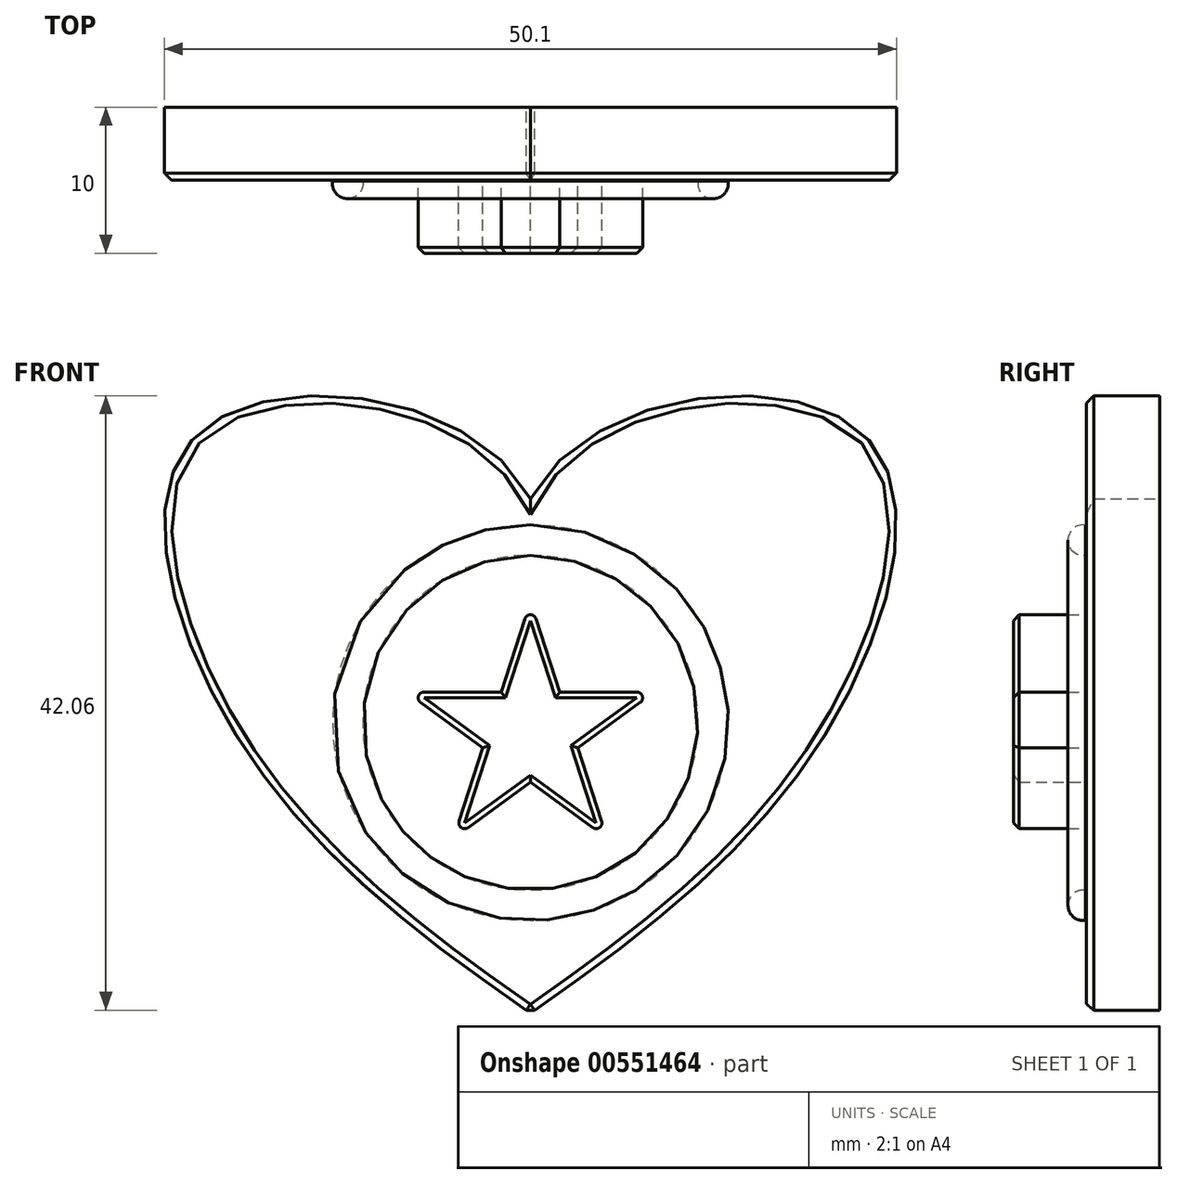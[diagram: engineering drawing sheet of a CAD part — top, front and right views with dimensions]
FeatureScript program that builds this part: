
annotation { "Feature Type Name" : "Feature", "Feature Type Description" : "" }
export const myFeature = defineFeature(function(context is Context, id is Id, definition is map)
    precondition{}
    {
        {
            var Q0;
            Q0=qCreatedBy(makeId("Front.planeOp"),FACE);
            var sketch = newSketch(context, id + "F0", { "sketchPlane" : qUnion([Q0])});
            skFitSpline(sketch, "E0", {"points": [v(0, 4.74) * mm, v(-22.34, 9.53) * mm, v(-20.92, -10.1) * mm, v(0, -30.47) * mm], "startDerivative": vector(-35.89, 67.68) * mm, "endDerivative": vector(70.46, -48.53) * mm});
            skFitSpline(sketch, "E1.MirrorCS", {"points": [v(0, 4.74) * mm, v(22.34, 9.53) * mm, v(20.92, -10.1) * mm, v(0, -30.47) * mm], "startDerivative": vector(35.89, 67.68) * mm, "endDerivative": vector(-70.46, -48.53) * mm});
            skPoint(sketch, "E2", {"position": v(-25, 1.75) * mm});
            skPoint(sketch, "E3", {"position": v(25, 1.75) * mm});
            skSolve(sketch);
        }
        {
            var Q0;
            Q0=makeQuery(id+"F0.imprint","IMPRINT",FACE,{"disambiguationData":[TD([[makeQuery(id+"F0.imprint","IMPRINT",EDGE,{"derivedFrom":sQuery(id+"F0.wireOp",EDGE,"E0")}),1.0]])]});
            extrude(context, id + "F1", {"entities" : qUnion([Q0]), "depth" : 5 * mm, "offsetDistance" : 25 * mm});
        }
        {
            var Q0;
            Q0=makeQuery(id+"F1.opExtrude","CAP_EDGE",EDGE,{"disambiguationData":[OSD([sQuery(id+"F0.wireOp",EDGE,"E1.MirrorCS")])],"isStart":false});
            var Q1;
            Q1=makeQuery(id+"F1.opExtrude","CAP_EDGE",EDGE,{"disambiguationData":[OSD([sQuery(id+"F0.wireOp",EDGE,"E0")])],"isStart":false});
            var Q2;
            {var subQ0=sQuery(id+"F0.wireOp",EDGE,"E1.MirrorCS");var subQ1=sQuery(id+"F0.wireOp",EDGE,"E0");Q2=makeQuery(id+"F1.opExtrude","SWEPT_EDGE",EDGE,{"disambiguationData":[OSD([subQ1,subQ0]),TDD([makeQuery(id+"F0.imprint","INTERSECT",VERTEX,{"disambiguationData":[OD(1.0)],"derivedFrom":[subQ1,subQ0]})])]});}
            chamfer(context, id + "F2", {"entities" : qUnion([Q0, Q1, Q2]), "width" : .5 * mm, "tangentPropagation" : true});
        }
        {
            var Q0;
            Q0=makeQuery(id+"F1.opExtrude","CAP_FACE",FACE,{"disambiguationData":[OSD([sQuery(id+"F0.wireOp",EDGE,"E0"),sQuery(id+"F0.wireOp",EDGE,"E1.MirrorCS")])],"isStart":false});
            var sketch = newSketch(context, id + "F3", { "sketchPlane" : qUnion([Q0])});
            skCircle(sketch, "E4", {"center": v(0, -10.6) * mm, "radius": 12.5 * mm});
            skSolve(sketch);
        }
        {
            var Q0;
            Q0=qCreatedBy(makeId("Right.planeOp"),FACE);
            var sketch = newSketch(context, id + "F4", { "sketchPlane" : qUnion([Q0])});
            skLineSegment(sketch, "E5", {"start": v(-5.07, 2.94) * mm, "end": v(-5.07, 0.87) * mm});
            skArc(sketch, "E6", {"start": v(-5.07, 2.94) * mm, "mid": v(-6.26, 1.9) * mm, "end": v(-5.07, 0.87) * mm});
            skSolve(sketch);
        }
        {
            var Q0;
            Q0=makeQuery(id+"F4.imprint","IMPRINT",FACE,{"disambiguationData":[TD([[makeQuery(id+"F4.imprint","IMPRINT",EDGE,{"derivedFrom":sQuery(id+"F4.wireOp",EDGE,"E5")}),-1.0]])]});
            var Q1;
            Q1=sQuery(id+"F3.wireOp",EDGE,"E4");
            sweep(context, id + "F5", {"operationType" : NewBodyOperationType.ADD, "profiles" : qUnion([Q0]), "path" : qUnion([Q1])});
        }
        {
            var Q0;
            Q0=makeQuery(id+"F1.opExtrude","CAP_FACE",FACE,{"disambiguationData":[OSD([sQuery(id+"F0.wireOp",EDGE,"E0"),sQuery(id+"F0.wireOp",EDGE,"E1.MirrorCS")])],"isStart":false});
            var sketch = newSketch(context, id + "F6", { "sketchPlane" : qUnion([Q0])});
            skLineSegment(sketch, "E7", {"start": v(-0.38, -3.48) * mm, "end": v(-2, -8.5) * mm});
            skLineSegment(sketch, "E8", {"start": v(-2, -8.5) * mm, "end": v(-7.28, -8.5) * mm});
            skLineSegment(sketch, "E9", {"start": v(-7.51, -9.21) * mm, "end": v(-3.25, -12.31) * mm});
            skLineSegment(sketch, "E10", {"start": v(-3.25, -12.31) * mm, "end": v(-4.88, -17.32) * mm});
            skLineSegment(sketch, "E11", {"start": v(-4.26, -17.77) * mm, "end": v(0, -14.67) * mm});
            skLineSegment(sketch, "E12.MirrorCS", {"start": v(0.38, -3.48) * mm, "end": v(2, -8.5) * mm});
            skLineSegment(sketch, "E13.MirrorCS", {"start": v(2, -8.5) * mm, "end": v(7.28, -8.5) * mm});
            skLineSegment(sketch, "E14.MirrorCS", {"start": v(7.51, -9.21) * mm, "end": v(3.25, -12.31) * mm});
            skLineSegment(sketch, "E15.MirrorCS", {"start": v(3.25, -12.31) * mm, "end": v(4.88, -17.32) * mm});
            skLineSegment(sketch, "E16.MirrorCS", {"start": v(4.26, -17.77) * mm, "end": v(0, -14.67) * mm});
            skPoint(sketch, "E17.visualSharp", {"position": v(5.26, -18.5) * mm});
            skArc(sketch, "E17.filletArc", {"start": v(4.26, -17.77) * mm, "mid": v(4.73, -17.77) * mm, "end": v(4.88, -17.32) * mm});
            skPoint(sketch, "E18.visualSharp", {"position": v(8.5, -8.5) * mm});
            skArc(sketch, "E18.filletArc", {"start": v(7.51, -9.21) * mm, "mid": v(7.66, -8.77) * mm, "end": v(7.28, -8.5) * mm});
            skPoint(sketch, "E19.visualSharp", {"position": v(0, -2.3) * mm});
            skArc(sketch, "E19.filletArc", {"start": v(0.38, -3.48) * mm, "mid": v(0, -3.2) * mm, "end": v(-0.38, -3.48) * mm});
            skPoint(sketch, "E20.visualSharp", {"position": v(-8.5, -8.5) * mm});
            skArc(sketch, "E20.filletArc", {"start": v(-7.28, -8.5) * mm, "mid": v(-7.66, -8.77) * mm, "end": v(-7.51, -9.21) * mm});
            skPoint(sketch, "E21.visualSharp", {"position": v(-5.26, -18.5) * mm});
            skArc(sketch, "E21.filletArc", {"start": v(-4.88, -17.32) * mm, "mid": v(-4.73, -17.77) * mm, "end": v(-4.26, -17.77) * mm});
            skSolve(sketch);
        }
        {
            var Q0;
            Q0=makeQuery(id+"F6.imprint","IMPRINT",FACE,{"disambiguationData":[TD([[makeQuery(id+"F6.imprint","IMPRINT",EDGE,{"derivedFrom":sQuery(id+"F6.wireOp",EDGE,"E7")}),1.0]])]});
            extrude(context, id + "F7", {"entities" : qUnion([Q0]), "operationType" : NewBodyOperationType.ADD, "depth" : 5 * mm, "offsetDistance" : 25 * mm});
        }
        {
            var Q0;
            Q0=makeQuery(id+"F7.opExtrude","CAP_EDGE",EDGE,{"disambiguationData":[OSD([sQuery(id+"F6.wireOp",EDGE,"E9")])],"isStart":false});
            var Q1;
            Q1=makeQuery(id+"F7.opExtrude","CAP_EDGE",EDGE,{"disambiguationData":[OSD([sQuery(id+"F6.wireOp",EDGE,"E10")])],"isStart":false});
            var Q2;
            Q2=makeQuery(id+"F7.opExtrude","CAP_EDGE",EDGE,{"disambiguationData":[OSD([sQuery(id+"F6.wireOp",EDGE,"E11")])],"isStart":false});
            var Q3;
            Q3=makeQuery(id+"F7.opExtrude","CAP_EDGE",EDGE,{"disambiguationData":[OSD([sQuery(id+"F6.wireOp",EDGE,"E16.MirrorCS")])],"isStart":false});
            var Q4;
            Q4=makeQuery(id+"F7.opExtrude","CAP_EDGE",EDGE,{"disambiguationData":[OSD([sQuery(id+"F6.wireOp",EDGE,"E15.MirrorCS")])],"isStart":false});
            var Q5;
            Q5=makeQuery(id+"F7.opExtrude","CAP_EDGE",EDGE,{"disambiguationData":[OSD([sQuery(id+"F6.wireOp",EDGE,"E14.MirrorCS")])],"isStart":false});
            var Q6;
            Q6=makeQuery(id+"F7.opExtrude","CAP_EDGE",EDGE,{"disambiguationData":[OSD([sQuery(id+"F6.wireOp",EDGE,"E13.MirrorCS")])],"isStart":false});
            var Q7;
            Q7=makeQuery(id+"F7.opExtrude","CAP_EDGE",EDGE,{"disambiguationData":[OSD([sQuery(id+"F6.wireOp",EDGE,"E12.MirrorCS")])],"isStart":false});
            var Q8;
            Q8=makeQuery(id+"F7.opExtrude","CAP_EDGE",EDGE,{"disambiguationData":[OSD([sQuery(id+"F6.wireOp",EDGE,"E7")])],"isStart":false});
            var Q9;
            Q9=makeQuery(id+"F7.opExtrude","CAP_EDGE",EDGE,{"disambiguationData":[OSD([sQuery(id+"F6.wireOp",EDGE,"E8")])],"isStart":false});
            chamfer(context, id + "F8", {"entities" : qUnion([Q0, Q1, Q2, Q3, Q4, Q5, Q6, Q7, Q8, Q9]), "width" : .4 * mm, "tangentPropagation" : true});
        }
    });
